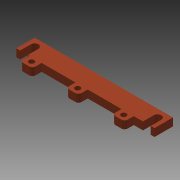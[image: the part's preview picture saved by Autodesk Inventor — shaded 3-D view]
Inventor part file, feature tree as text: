
AUTODESK INVENTOR PART (.ipt)
format: ipt  version: 2013 (Build 170138000, 138)  size: 172,032 bytes
history: native  units: in
note: dims shown in document units (in); Inventor stores cm internally (conversion verified against a paired STEP export)
features: fillet x6, extrude x3, sketch x3
ambient origin geometry x8: Origin, YZ Plane, XZ Plane, XY Plane, X Axis, Y Axis, Z Axis, Center Point
bodies: Solid1 (feature_tree)
feature tree (12):
  extrude  "Extrusion1"  Depth=0.4724in
  fillet  "Fillet1"  Radius=0.8465in
  fillet  "Fillet2"  Radius=1.1811in
  fillet  "Fillet3"  Radius=1.1811in
  fillet  "Fillet4"  Radius=0.2362in
  fillet  "Fillet5"  Radius=0.2362in
  fillet  "Fillet6"  Radius=0.2362in
  extrude  "Extrusion2"  Depth=0.315in
  extrude  "Extrusion4"  Depth=0.1969in TaperAngle=0.0deg
  sketch  "Sketch1"  dims[d0=3.5433in d3=0.4724in d4=0.8465in d5=1.1811in d6=1.1811in d7=0.2362in d8=0.2362in d9=0.2362in]
  sketch  "Sketch2"  dims[d10=0.315in d11=0.315in]
  sketch  "Sketch4"  dims[d12=0.315in d13=0.1969in d14=0.0in d15=0.0787in d16=0.0787in d17=0.0787in d18=0.0787in d19=0.0787in d20=0.0787in d23=0.1378in d29=0.1378in d30=0.1378in d31=0.3937in d32=0.0in d47=0.0984in d48=0.1575in d49=0.0984in d50=0.1575in d51=0.0984in d52=0.1575in d53=0.1969in d54=0.1969in d55=0.1969in d56=0.1969in d57=0.1969in d58=0.1969in d59=0.3937in d60=0.0in]
